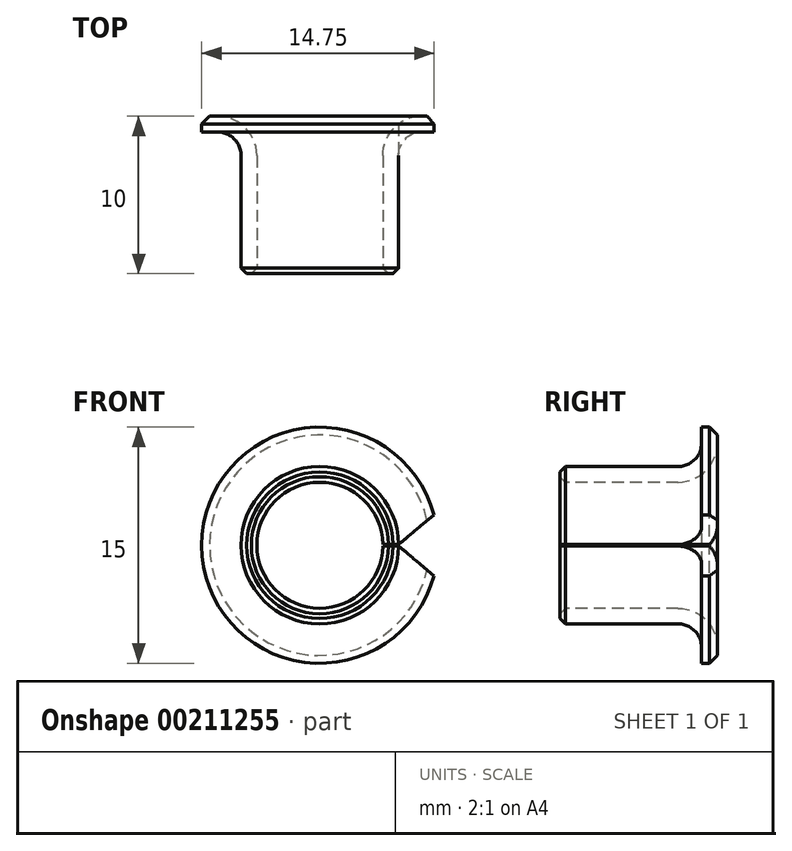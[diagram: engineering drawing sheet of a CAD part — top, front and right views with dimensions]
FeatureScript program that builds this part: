
annotation { "Feature Type Name" : "Feature", "Feature Type Description" : "" }
export const myFeature = defineFeature(function(context is Context, id is Id, definition is map)
    precondition{}
    {
        {
            var Q0;
            Q0=qCreatedBy(makeId("Right.planeOp"),FACE);
            var sketch = newSketch(context, id + "F0", { "sketchPlane" : qUnion([Q0])});
            skLineSegment(sketch, "E0", {"start": v(-5, 0) * mm, "end": v(5, 0) * mm, "construction": true});
            skLineSegment(sketch, "E1", {"start": v(5, 0) * mm, "end": v(5, 4) * mm, "construction": true});
            skLineSegment(sketch, "E2", {"start": v(5, 7.5) * mm, "end": v(5, 4) * mm});
            skLineSegment(sketch, "E3", {"start": v(-5, 4) * mm, "end": v(-5, 5) * mm});
            skLineSegment(sketch, "E4", {"start": v(-5, 5) * mm, "end": v(4, 5) * mm});
            skLineSegment(sketch, "E5", {"start": v(4, 5) * mm, "end": v(4, 7.5) * mm});
            skLineSegment(sketch, "E6", {"start": v(4, 7.5) * mm, "end": v(5, 7.5) * mm});
            skLineSegment(sketch, "E7", {"start": v(5, 4) * mm, "end": v(-5, 4) * mm});
            skSolve(sketch);
        }
        {
            var Q0;
            Q0=makeQuery(id+"F0.imprint","IMPRINT",FACE,{"disambiguationData":[TD([[makeQuery(id+"F0.imprint","IMPRINT",EDGE,{"derivedFrom":sQuery(id+"F0.wireOp",EDGE,"E2")}),-1.0]])]});
            var Q1;
            Q1=sQuery(id+"F0.wireOp",EDGE,"E0");
            revolve(context, id + "F1", {"entities" : qUnion([Q0]), "axis" : qUnion([Q1]), "revolveType" : RevolveType.FULL});
        }
        {
            var Q0;
            Q0=makeQuery(id+"F1.opRevolve","SWEPT_EDGE",EDGE,{"disambiguationData":[OSD([sQuery(id+"F0.wireOp",EDGE,"E3"),sQuery(id+"F0.wireOp",EDGE,"E4")])]});
            var Q1;
            Q1=makeQuery(id+"F1.opRevolve","SWEPT_EDGE",EDGE,{"disambiguationData":[OSD([sQuery(id+"F0.wireOp",EDGE,"E3"),sQuery(id+"F0.wireOp",EDGE,"E7")])]});
            chamfer(context, id + "F2", {"entities" : qUnion([Q0, Q1]), "width" : .35 * mm, "tangentPropagation" : true});
        }
        {
            var Q0;
            Q0=makeQuery(id+"F1.opRevolve","SWEPT_EDGE",EDGE,{"disambiguationData":[OSD([sQuery(id+"F0.wireOp",EDGE,"E4"),sQuery(id+"F0.wireOp",EDGE,"E5")])]});
            fillet(context, id + "F3", {"entities" : qUnion([Q0]), "radius" : 1.5 * mm, "tangentPropagation" : true, "allowEdgeOverflow" : false});
        }
        {
            var Q0;
            Q0=makeQuery(id+"F1.opRevolve","SWEPT_EDGE",EDGE,{"disambiguationData":[OSD([sQuery(id+"F0.wireOp",EDGE,"E2"),sQuery(id+"F0.wireOp",EDGE,"E7")])]});
            fillet(context, id + "F4", {"entities" : qUnion([Q0]), "radius" : 2.5 * mm, "tangentPropagation" : true, "allowEdgeOverflow" : false});
        }
        {
            var Q0;
            Q0=makeQuery(id+"F1.opRevolve","SWEPT_EDGE",EDGE,{"disambiguationData":[OSD([sQuery(id+"F0.wireOp",EDGE,"E2"),sQuery(id+"F0.wireOp",EDGE,"E6")])]});
            chamfer(context, id + "F5", {"entities" : qUnion([Q0]), "width" : .5 * mm, "tangentPropagation" : true});
        }
        {
            var Q0;
            Q0=makeQuery(id+"F1.opRevolve","SWEPT_FACE",FACE,{"disambiguationData":[OSD([sQuery(id+"F0.wireOp",EDGE,"E3")])]});
            var sketch = newSketch(context, id + "F6", { "sketchPlane" : qUnion([Q0])});
            skLineSegment(sketch, "E8", {"start": v(0, 0) * mm, "end": v(4, 0) * mm, "construction": true});
            skLineSegment(sketch, "E9", {"start": v(4, 0.05) * mm, "end": v(5, 0.05) * mm});
            skLineSegment(sketch, "E10", {"start": v(4, -0.05) * mm, "end": v(5, -0.05) * mm});
            skLineSegment(sketch, "E11", {"start": v(4, 0.05) * mm, "end": v(4, -0.05) * mm});
            skLineSegment(sketch, "E12", {"start": v(5, 0.05) * mm, "end": v(8, 2.57) * mm});
            skLineSegment(sketch, "E13", {"start": v(8, 2.57) * mm, "end": v(8, -2.57) * mm});
            skLineSegment(sketch, "E14", {"start": v(8, -2.57) * mm, "end": v(5, -0.05) * mm});
            skSolve(sketch);
        }
        {
            var Q0;
            {var subQ0=sQuery(id+"F6.wireOp",EDGE,"E12");Q0=makeQuery(id+"F6.imprint","IMPRINT",FACE,{"disambiguationData":[TD([[makeQuery(id+"F6.imprint","IMPRINT",EDGE,{"derivedFrom":subQ0}),-1.0]])]});}
            var Q1;
            {var subQ0=sQuery(id+"F6.wireOp",EDGE,"E11");Q1=makeQuery(id+"F6.imprint","IMPRINT",FACE,{"disambiguationData":[TD([[makeQuery(id+"F6.imprint","IMPRINT",EDGE,{"derivedFrom":subQ0}),1.0]])]});}
            var Q2;
            {var subQ0=sQuery(id+"F6.wireOp",EDGE,"E9");var subQ1=sQuery(id+"F0.wireOp",EDGE,"E3");var subQ2=makeQuery(id+"F1.opRevolve","SWEPT_FACE",FACE,{"disambiguationData":[OSD([subQ1])]});var subQ3=makeQuery(id+"F2.opChamfer","BLEND_EDGE",EDGE,{"blendedFrom":[makeQuery(id+"F1.opRevolve","SWEPT_EDGE",EDGE,{"disambiguationData":[OSD([subQ1,sQuery(id+"F0.wireOp",EDGE,"E4")])]}),subQ2],"blendedInto":[subQ2]});var subQ4=makeQuery(id+"F6.imprint","INTERSECT",VERTEX,{"derivedFrom":[subQ3,subQ0]});Q2=makeQuery(id+"F6.imprint","IMPRINT",FACE,{"disambiguationData":[TD([[makeQuery(id+"F6.imprint","IMPRINT",EDGE,{"disambiguationData":[TD([[subQ4,1.0]])],"derivedFrom":subQ0}),-1.0]])]});}
            extrude(context, id + "F7", {"entities" : qUnion([Q0, Q1, Q2]), "operationType" : NewBodyOperationType.REMOVE, "endBound" : BoundingType.UP_TO_NEXT, "oppositeDirection" : true, "depth" : 25 * mm});
        }
    });
